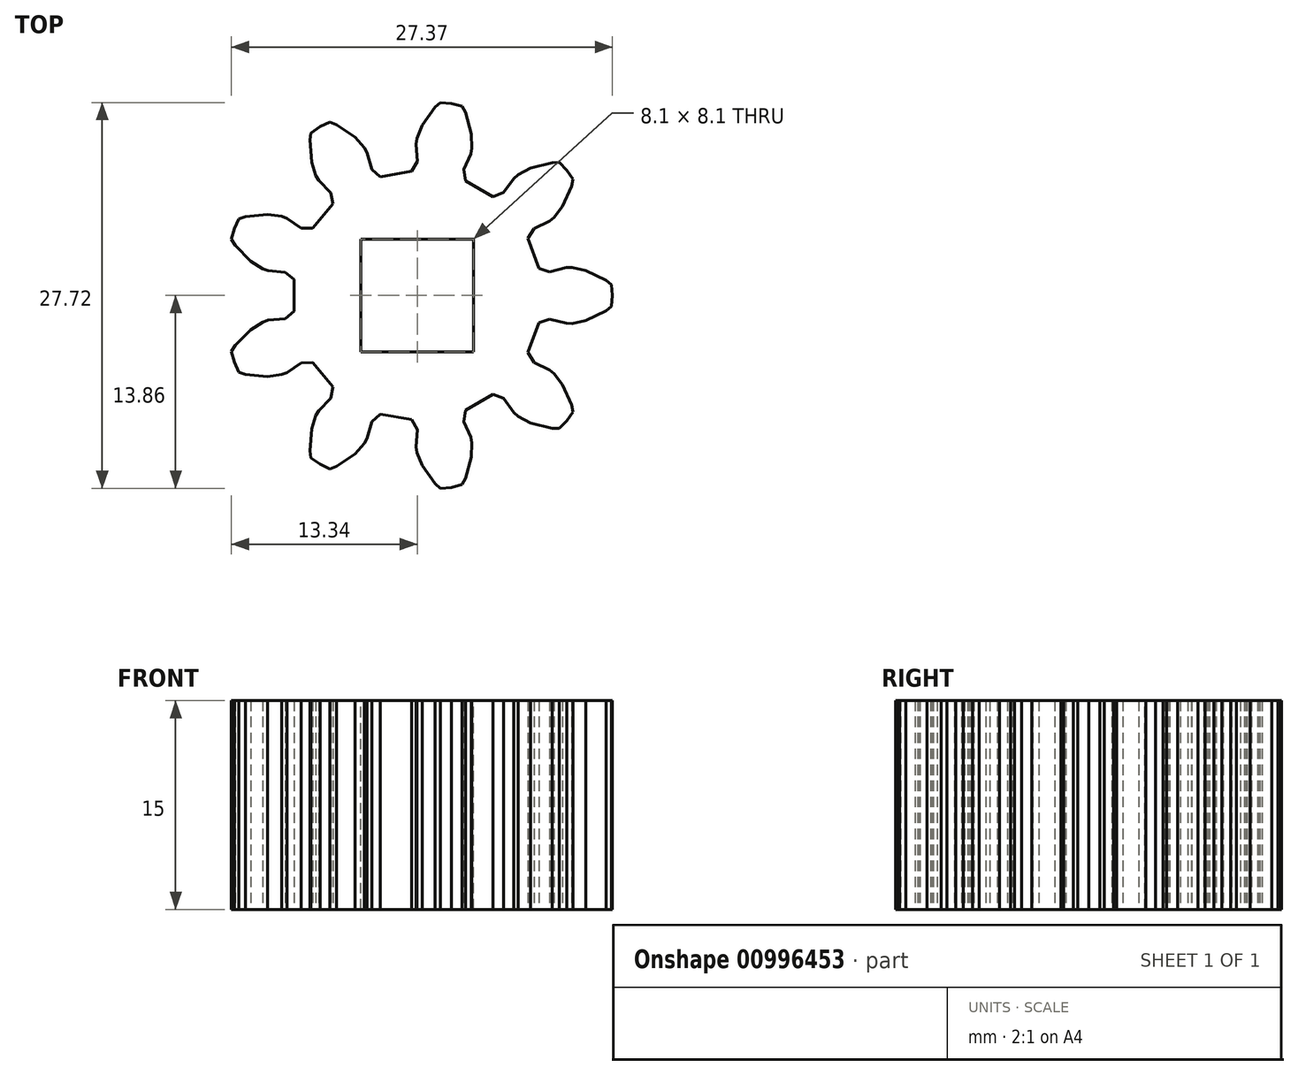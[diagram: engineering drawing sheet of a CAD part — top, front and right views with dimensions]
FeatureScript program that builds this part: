
annotation { "Feature Type Name" : "Feature", "Feature Type Description" : "" }
export const myFeature = defineFeature(function(context is Context, id is Id, definition is map)
    precondition{}
    {
        {
            var Q0;
            Q0=qCreatedBy(makeId("Top.planeOp"),FACE);
            var sketch = newSketch(context, id + "F0", { "sketchPlane" : qUnion([Q0])});
            skLineSegment(sketch, "E0", {"start": v(10.2, -9.56) * mm, "end": v(10.75, -9) * mm});
            skLineSegment(sketch, "E1", {"start": v(10.75, -9) * mm, "end": v(11.2, -8.36) * mm});
            skLineSegment(sketch, "E2", {"start": v(11.2, -8.36) * mm, "end": v(11.1, -7.86) * mm});
            skLineSegment(sketch, "E3", {"start": v(11.1, -7.86) * mm, "end": v(10.44, -6.4) * mm});
            skLineSegment(sketch, "E4", {"start": v(10.44, -6.4) * mm, "end": v(9.83, -5.6) * mm});
            skLineSegment(sketch, "E5", {"start": v(9.83, -5.6) * mm, "end": v(9.5, -5.34) * mm});
            skLineSegment(sketch, "E6", {"start": v(9.5, -5.34) * mm, "end": v(8.38, -4.8) * mm});
            skLineSegment(sketch, "E7", {"start": v(8.38, -4.8) * mm, "end": v(7.96, -4.1) * mm});
            skLineSegment(sketch, "E8", {"start": v(7.96, -4.1) * mm, "end": v(8.74, -1.96) * mm});
            skLineSegment(sketch, "E9", {"start": v(8.74, -1.96) * mm, "end": v(9.52, -1.7) * mm});
            skLineSegment(sketch, "E10", {"start": v(9.52, -1.7) * mm, "end": v(10.72, -2) * mm});
            skLineSegment(sketch, "E11", {"start": v(10.72, -2) * mm, "end": v(11.13, -2) * mm});
            skLineSegment(sketch, "E12", {"start": v(11.13, -2) * mm, "end": v(12.12, -1.8) * mm});
            skLineSegment(sketch, "E13", {"start": v(12.12, -1.8) * mm, "end": v(13.56, -1.1) * mm});
            skLineSegment(sketch, "E14", {"start": v(13.56, -1.1) * mm, "end": v(13.96, -0.79) * mm});
            skLineSegment(sketch, "E15", {"start": v(13.96, -0.79) * mm, "end": v(14.03, 0) * mm});
            skLineSegment(sketch, "E16", {"start": v(14.03, 0) * mm, "end": v(13.96, 0.79) * mm});
            skLineSegment(sketch, "E17", {"start": v(13.96, 0.79) * mm, "end": v(13.56, 1.1) * mm});
            skLineSegment(sketch, "E18", {"start": v(13.56, 1.1) * mm, "end": v(12.12, 1.8) * mm});
            skLineSegment(sketch, "E19", {"start": v(12.12, 1.8) * mm, "end": v(11.13, 2) * mm});
            skLineSegment(sketch, "E20", {"start": v(11.13, 2) * mm, "end": v(10.72, 2) * mm});
            skLineSegment(sketch, "E21", {"start": v(10.72, 2) * mm, "end": v(9.52, 1.7) * mm});
            skLineSegment(sketch, "E22", {"start": v(9.52, 1.7) * mm, "end": v(8.74, 1.96) * mm});
            skLineSegment(sketch, "E23", {"start": v(8.74, 1.96) * mm, "end": v(7.96, 4.1) * mm});
            skLineSegment(sketch, "E24", {"start": v(7.96, 4.1) * mm, "end": v(8.38, 4.8) * mm});
            skLineSegment(sketch, "E25", {"start": v(8.38, 4.8) * mm, "end": v(9.5, 5.34) * mm});
            skLineSegment(sketch, "E26", {"start": v(9.5, 5.34) * mm, "end": v(9.83, 5.6) * mm});
            skLineSegment(sketch, "E27", {"start": v(9.83, 5.6) * mm, "end": v(10.44, 6.4) * mm});
            skLineSegment(sketch, "E28", {"start": v(10.44, 6.4) * mm, "end": v(11.1, 7.86) * mm});
            skLineSegment(sketch, "E29", {"start": v(11.1, 7.86) * mm, "end": v(11.2, 8.36) * mm});
            skLineSegment(sketch, "E30", {"start": v(11.2, 8.36) * mm, "end": v(10.75, 9) * mm});
            skLineSegment(sketch, "E31", {"start": v(10.75, 9) * mm, "end": v(10.2, 9.56) * mm});
            skLineSegment(sketch, "E32", {"start": v(10.2, 9.56) * mm, "end": v(9.68, 9.55) * mm});
            skLineSegment(sketch, "E33", {"start": v(9.68, 9.55) * mm, "end": v(8.14, 9.15) * mm});
            skLineSegment(sketch, "E34", {"start": v(8.14, 9.15) * mm, "end": v(7.24, 8.68) * mm});
            skLineSegment(sketch, "E35", {"start": v(7.24, 8.68) * mm, "end": v(6.93, 8.4) * mm});
            skLineSegment(sketch, "E36", {"start": v(6.93, 8.4) * mm, "end": v(6.2, 7.4) * mm});
            skLineSegment(sketch, "E37", {"start": v(6.2, 7.4) * mm, "end": v(5.44, 7.1) * mm});
            skLineSegment(sketch, "E38", {"start": v(5.44, 7.1) * mm, "end": v(3.47, 8.24) * mm});
            skLineSegment(sketch, "E39", {"start": v(3.47, 8.24) * mm, "end": v(3.34, 9.06) * mm});
            skLineSegment(sketch, "E40", {"start": v(3.34, 9.06) * mm, "end": v(3.85, 10.18) * mm});
            skLineSegment(sketch, "E41", {"start": v(3.85, 10.18) * mm, "end": v(3.93, 10.6) * mm});
            skLineSegment(sketch, "E42", {"start": v(3.93, 10.6) * mm, "end": v(3.89, 11.6) * mm});
            skLineSegment(sketch, "E43", {"start": v(3.89, 11.6) * mm, "end": v(3.46, 13.14) * mm});
            skLineSegment(sketch, "E44", {"start": v(3.46, 13.14) * mm, "end": v(3.22, 13.59) * mm});
            skLineSegment(sketch, "E45", {"start": v(3.22, 13.59) * mm, "end": v(2.45, 13.8) * mm});
            skLineSegment(sketch, "E46", {"start": v(2.45, 13.8) * mm, "end": v(1.67, 13.86) * mm});
            skLineSegment(sketch, "E47", {"start": v(1.67, 13.86) * mm, "end": v(1.28, 13.53) * mm});
            skLineSegment(sketch, "E48", {"start": v(1.28, 13.53) * mm, "end": v(0.35, 12.23) * mm});
            skLineSegment(sketch, "E49", {"start": v(0.35, 12.23) * mm, "end": v(-0.03, 11.3) * mm});
            skLineSegment(sketch, "E50", {"start": v(-0.03, 11.3) * mm, "end": v(-0.1, 10.88) * mm});
            skLineSegment(sketch, "E51", {"start": v(-0.1, 10.88) * mm, "end": v(0, 9.65) * mm});
            skLineSegment(sketch, "E52", {"start": v(0, 9.65) * mm, "end": v(-0.4, 8.93) * mm});
            skLineSegment(sketch, "E53", {"start": v(-0.4, 8.93) * mm, "end": v(-2.64, 8.53) * mm});
            skLineSegment(sketch, "E54", {"start": v(-2.64, 8.53) * mm, "end": v(-3.26, 9.07) * mm});
            skLineSegment(sketch, "E55", {"start": v(-3.26, 9.07) * mm, "end": v(-3.6, 10.26) * mm});
            skLineSegment(sketch, "E56", {"start": v(-3.6, 10.26) * mm, "end": v(-3.8, 10.63) * mm});
            skLineSegment(sketch, "E57", {"start": v(-3.8, 10.63) * mm, "end": v(-4.47, 11.38) * mm});
            skLineSegment(sketch, "E58", {"start": v(-4.47, 11.38) * mm, "end": v(-5.8, 12.28) * mm});
            skLineSegment(sketch, "E59", {"start": v(-5.8, 12.28) * mm, "end": v(-6.27, 12.46) * mm});
            skLineSegment(sketch, "E60", {"start": v(-6.27, 12.46) * mm, "end": v(-6.98, 12.13) * mm});
            skLineSegment(sketch, "E61", {"start": v(-6.98, 12.13) * mm, "end": v(-7.63, 11.68) * mm});
            skLineSegment(sketch, "E62", {"start": v(-7.63, 11.68) * mm, "end": v(-7.7, 11.17) * mm});
            skLineSegment(sketch, "E63", {"start": v(-7.7, 11.17) * mm, "end": v(-7.58, 9.58) * mm});
            skLineSegment(sketch, "E64", {"start": v(-7.58, 9.58) * mm, "end": v(-7.27, 8.62) * mm});
            skLineSegment(sketch, "E65", {"start": v(-7.27, 8.62) * mm, "end": v(-7.06, 8.26) * mm});
            skLineSegment(sketch, "E66", {"start": v(-7.06, 8.26) * mm, "end": v(-6.2, 7.38) * mm});
            skLineSegment(sketch, "E67", {"start": v(-6.2, 7.38) * mm, "end": v(-6.04, 6.57) * mm});
            skLineSegment(sketch, "E68", {"start": v(-6.04, 6.57) * mm, "end": v(-7.5, 4.82) * mm});
            skLineSegment(sketch, "E69", {"start": v(-7.5, 4.82) * mm, "end": v(-8.32, 4.84) * mm});
            skLineSegment(sketch, "E70", {"start": v(-8.32, 4.84) * mm, "end": v(-9.34, 5.54) * mm});
            skLineSegment(sketch, "E71", {"start": v(-9.34, 5.54) * mm, "end": v(-9.73, 5.69) * mm});
            skLineSegment(sketch, "E72", {"start": v(-9.73, 5.69) * mm, "end": v(-10.73, 5.82) * mm});
            skLineSegment(sketch, "E73", {"start": v(-10.73, 5.82) * mm, "end": v(-12.32, 5.67) * mm});
            skLineSegment(sketch, "E74", {"start": v(-12.32, 5.67) * mm, "end": v(-12.8, 5.5) * mm});
            skLineSegment(sketch, "E75", {"start": v(-12.8, 5.5) * mm, "end": v(-13.14, 4.8) * mm});
            skLineSegment(sketch, "E76", {"start": v(-13.14, 4.8) * mm, "end": v(-13.34, 4.03) * mm});
            skLineSegment(sketch, "E77", {"start": v(-13.34, 4.03) * mm, "end": v(-13.08, 3.6) * mm});
            skLineSegment(sketch, "E78", {"start": v(-13.08, 3.6) * mm, "end": v(-11.96, 2.45) * mm});
            skLineSegment(sketch, "E79", {"start": v(-11.96, 2.45) * mm, "end": v(-11.1, 1.91) * mm});
            skLineSegment(sketch, "E80", {"start": v(-11.1, 1.91) * mm, "end": v(-10.71, 1.78) * mm});
            skLineSegment(sketch, "E81", {"start": v(-10.71, 1.78) * mm, "end": v(-9.48, 1.66) * mm});
            skLineSegment(sketch, "E82", {"start": v(-9.48, 1.66) * mm, "end": v(-8.84, 1.14) * mm});
            skLineSegment(sketch, "E83", {"start": v(-8.84, 1.14) * mm, "end": v(-8.84, -1.14) * mm});
            skLineSegment(sketch, "E84", {"start": v(-8.84, -1.14) * mm, "end": v(-9.48, -1.66) * mm});
            skLineSegment(sketch, "E85", {"start": v(-9.48, -1.66) * mm, "end": v(-10.71, -1.78) * mm});
            skLineSegment(sketch, "E86", {"start": v(-10.71, -1.78) * mm, "end": v(-11.1, -1.91) * mm});
            skLineSegment(sketch, "E87", {"start": v(-11.1, -1.91) * mm, "end": v(-11.96, -2.45) * mm});
            skLineSegment(sketch, "E88", {"start": v(-11.96, -2.45) * mm, "end": v(-13.08, -3.6) * mm});
            skLineSegment(sketch, "E89", {"start": v(-13.08, -3.6) * mm, "end": v(-13.34, -4.03) * mm});
            skLineSegment(sketch, "E90", {"start": v(-13.34, -4.03) * mm, "end": v(-13.14, -4.8) * mm});
            skLineSegment(sketch, "E91", {"start": v(-13.14, -4.8) * mm, "end": v(-12.8, -5.5) * mm});
            skLineSegment(sketch, "E92", {"start": v(-12.8, -5.5) * mm, "end": v(-12.32, -5.67) * mm});
            skLineSegment(sketch, "E93", {"start": v(-12.32, -5.67) * mm, "end": v(-10.73, -5.82) * mm});
            skLineSegment(sketch, "E94", {"start": v(-10.73, -5.82) * mm, "end": v(-9.73, -5.69) * mm});
            skLineSegment(sketch, "E95", {"start": v(-9.73, -5.69) * mm, "end": v(-9.34, -5.54) * mm});
            skLineSegment(sketch, "E96", {"start": v(-9.34, -5.54) * mm, "end": v(-8.32, -4.84) * mm});
            skLineSegment(sketch, "E97", {"start": v(-8.32, -4.84) * mm, "end": v(-7.5, -4.82) * mm});
            skLineSegment(sketch, "E98", {"start": v(-7.5, -4.82) * mm, "end": v(-6.04, -6.57) * mm});
            skLineSegment(sketch, "E99", {"start": v(-6.04, -6.57) * mm, "end": v(-6.2, -7.38) * mm});
            skLineSegment(sketch, "E100", {"start": v(-6.2, -7.38) * mm, "end": v(-7.06, -8.26) * mm});
            skLineSegment(sketch, "E101", {"start": v(-7.06, -8.26) * mm, "end": v(-7.27, -8.62) * mm});
            skLineSegment(sketch, "E102", {"start": v(-7.27, -8.62) * mm, "end": v(-7.58, -9.58) * mm});
            skLineSegment(sketch, "E103", {"start": v(-7.58, -9.58) * mm, "end": v(-7.7, -11.17) * mm});
            skLineSegment(sketch, "E104", {"start": v(-7.7, -11.17) * mm, "end": v(-7.63, -11.68) * mm});
            skLineSegment(sketch, "E105", {"start": v(-7.63, -11.68) * mm, "end": v(-6.98, -12.13) * mm});
            skLineSegment(sketch, "E106", {"start": v(-6.98, -12.13) * mm, "end": v(-6.27, -12.46) * mm});
            skLineSegment(sketch, "E107", {"start": v(-6.27, -12.46) * mm, "end": v(-5.8, -12.28) * mm});
            skLineSegment(sketch, "E108", {"start": v(-5.8, -12.28) * mm, "end": v(-4.47, -11.38) * mm});
            skLineSegment(sketch, "E109", {"start": v(-4.47, -11.38) * mm, "end": v(-3.8, -10.63) * mm});
            skLineSegment(sketch, "E110", {"start": v(-3.8, -10.63) * mm, "end": v(-3.6, -10.26) * mm});
            skLineSegment(sketch, "E111", {"start": v(-3.6, -10.26) * mm, "end": v(-3.26, -9.07) * mm});
            skLineSegment(sketch, "E112", {"start": v(-3.26, -9.07) * mm, "end": v(-2.64, -8.53) * mm});
            skLineSegment(sketch, "E113", {"start": v(-2.64, -8.53) * mm, "end": v(-0.4, -8.93) * mm});
            skLineSegment(sketch, "E114", {"start": v(-0.4, -8.93) * mm, "end": v(0, -9.65) * mm});
            skLineSegment(sketch, "E115", {"start": v(0, -9.65) * mm, "end": v(-0.1, -10.88) * mm});
            skLineSegment(sketch, "E116", {"start": v(-0.1, -10.88) * mm, "end": v(-0.03, -11.3) * mm});
            skLineSegment(sketch, "E117", {"start": v(-0.03, -11.3) * mm, "end": v(0.35, -12.23) * mm});
            skLineSegment(sketch, "E118", {"start": v(0.35, -12.23) * mm, "end": v(1.28, -13.53) * mm});
            skLineSegment(sketch, "E119", {"start": v(1.28, -13.53) * mm, "end": v(1.67, -13.86) * mm});
            skLineSegment(sketch, "E120", {"start": v(1.67, -13.86) * mm, "end": v(2.45, -13.8) * mm});
            skLineSegment(sketch, "E121", {"start": v(2.45, -13.8) * mm, "end": v(3.22, -13.59) * mm});
            skLineSegment(sketch, "E122", {"start": v(3.22, -13.59) * mm, "end": v(3.46, -13.14) * mm});
            skLineSegment(sketch, "E123", {"start": v(3.46, -13.14) * mm, "end": v(3.89, -11.6) * mm});
            skLineSegment(sketch, "E124", {"start": v(3.89, -11.6) * mm, "end": v(3.93, -10.6) * mm});
            skLineSegment(sketch, "E125", {"start": v(3.93, -10.6) * mm, "end": v(3.85, -10.18) * mm});
            skLineSegment(sketch, "E126", {"start": v(3.85, -10.18) * mm, "end": v(3.34, -9.06) * mm});
            skLineSegment(sketch, "E127", {"start": v(3.34, -9.06) * mm, "end": v(3.47, -8.24) * mm});
            skLineSegment(sketch, "E128", {"start": v(3.47, -8.24) * mm, "end": v(5.44, -7.1) * mm});
            skLineSegment(sketch, "E129", {"start": v(5.44, -7.1) * mm, "end": v(6.2, -7.4) * mm});
            skLineSegment(sketch, "E130", {"start": v(6.2, -7.4) * mm, "end": v(6.93, -8.4) * mm});
            skLineSegment(sketch, "E131", {"start": v(6.93, -8.4) * mm, "end": v(7.24, -8.68) * mm});
            skLineSegment(sketch, "E132", {"start": v(7.24, -8.68) * mm, "end": v(8.14, -9.15) * mm});
            skLineSegment(sketch, "E133", {"start": v(8.14, -9.15) * mm, "end": v(9.68, -9.55) * mm});
            skLineSegment(sketch, "E134", {"start": v(9.68, -9.55) * mm, "end": v(10.2, -9.56) * mm});
            skSolve(sketch);
        }
        {
            var Q0;
            Q0=qSketchRegion(id+"F0",true);
            extrude(context, id + "F1", {"entities" : qUnion([Q0]), "depth" : 15 * mm, "offsetDistance" : 25.4 * mm});
        }
        {
            var Q0;
            Q0=makeQuery(id+"F1.opExtrude","CAP_FACE",FACE,{"disambiguationData":[OSD([sQuery(id+"F0.wireOp",EDGE,"E0"),sQuery(id+"F0.wireOp",EDGE,"E1"),sQuery(id+"F0.wireOp",EDGE,"E2"),sQuery(id+"F0.wireOp",EDGE,"E3"),sQuery(id+"F0.wireOp",EDGE,"E4"),sQuery(id+"F0.wireOp",EDGE,"E5"),sQuery(id+"F0.wireOp",EDGE,"E6"),sQuery(id+"F0.wireOp",EDGE,"E7"),sQuery(id+"F0.wireOp",EDGE,"E8"),sQuery(id+"F0.wireOp",EDGE,"E9"),sQuery(id+"F0.wireOp",EDGE,"E10"),sQuery(id+"F0.wireOp",EDGE,"E11"),sQuery(id+"F0.wireOp",EDGE,"E12"),sQuery(id+"F0.wireOp",EDGE,"E13"),sQuery(id+"F0.wireOp",EDGE,"E14"),sQuery(id+"F0.wireOp",EDGE,"E15"),sQuery(id+"F0.wireOp",EDGE,"E16"),sQuery(id+"F0.wireOp",EDGE,"E17"),sQuery(id+"F0.wireOp",EDGE,"E18"),sQuery(id+"F0.wireOp",EDGE,"E19"),sQuery(id+"F0.wireOp",EDGE,"E20"),sQuery(id+"F0.wireOp",EDGE,"E21"),sQuery(id+"F0.wireOp",EDGE,"E22"),sQuery(id+"F0.wireOp",EDGE,"E23"),sQuery(id+"F0.wireOp",EDGE,"E24"),sQuery(id+"F0.wireOp",EDGE,"E25"),sQuery(id+"F0.wireOp",EDGE,"E26"),sQuery(id+"F0.wireOp",EDGE,"E27"),sQuery(id+"F0.wireOp",EDGE,"E28"),sQuery(id+"F0.wireOp",EDGE,"E29"),sQuery(id+"F0.wireOp",EDGE,"E30"),sQuery(id+"F0.wireOp",EDGE,"E31"),sQuery(id+"F0.wireOp",EDGE,"E32"),sQuery(id+"F0.wireOp",EDGE,"E33"),sQuery(id+"F0.wireOp",EDGE,"E34"),sQuery(id+"F0.wireOp",EDGE,"E35"),sQuery(id+"F0.wireOp",EDGE,"E36"),sQuery(id+"F0.wireOp",EDGE,"E37"),sQuery(id+"F0.wireOp",EDGE,"E38"),sQuery(id+"F0.wireOp",EDGE,"E39"),sQuery(id+"F0.wireOp",EDGE,"E40"),sQuery(id+"F0.wireOp",EDGE,"E41"),sQuery(id+"F0.wireOp",EDGE,"E42"),sQuery(id+"F0.wireOp",EDGE,"E43"),sQuery(id+"F0.wireOp",EDGE,"E44"),sQuery(id+"F0.wireOp",EDGE,"E45"),sQuery(id+"F0.wireOp",EDGE,"E46"),sQuery(id+"F0.wireOp",EDGE,"E47"),sQuery(id+"F0.wireOp",EDGE,"E48"),sQuery(id+"F0.wireOp",EDGE,"E49"),sQuery(id+"F0.wireOp",EDGE,"E50"),sQuery(id+"F0.wireOp",EDGE,"E51"),sQuery(id+"F0.wireOp",EDGE,"E52"),sQuery(id+"F0.wireOp",EDGE,"E53"),sQuery(id+"F0.wireOp",EDGE,"E54"),sQuery(id+"F0.wireOp",EDGE,"E55"),sQuery(id+"F0.wireOp",EDGE,"E56"),sQuery(id+"F0.wireOp",EDGE,"E57"),sQuery(id+"F0.wireOp",EDGE,"E58"),sQuery(id+"F0.wireOp",EDGE,"E59"),sQuery(id+"F0.wireOp",EDGE,"E60"),sQuery(id+"F0.wireOp",EDGE,"E61"),sQuery(id+"F0.wireOp",EDGE,"E62"),sQuery(id+"F0.wireOp",EDGE,"E63"),sQuery(id+"F0.wireOp",EDGE,"E64"),sQuery(id+"F0.wireOp",EDGE,"E65"),sQuery(id+"F0.wireOp",EDGE,"E66"),sQuery(id+"F0.wireOp",EDGE,"E67"),sQuery(id+"F0.wireOp",EDGE,"E68"),sQuery(id+"F0.wireOp",EDGE,"E69"),sQuery(id+"F0.wireOp",EDGE,"E70"),sQuery(id+"F0.wireOp",EDGE,"E71"),sQuery(id+"F0.wireOp",EDGE,"E72"),sQuery(id+"F0.wireOp",EDGE,"E73"),sQuery(id+"F0.wireOp",EDGE,"E74"),sQuery(id+"F0.wireOp",EDGE,"E75"),sQuery(id+"F0.wireOp",EDGE,"E76"),sQuery(id+"F0.wireOp",EDGE,"E77"),sQuery(id+"F0.wireOp",EDGE,"E78"),sQuery(id+"F0.wireOp",EDGE,"E79"),sQuery(id+"F0.wireOp",EDGE,"E80"),sQuery(id+"F0.wireOp",EDGE,"E81"),sQuery(id+"F0.wireOp",EDGE,"E82"),sQuery(id+"F0.wireOp",EDGE,"E83"),sQuery(id+"F0.wireOp",EDGE,"E84"),sQuery(id+"F0.wireOp",EDGE,"E85"),sQuery(id+"F0.wireOp",EDGE,"E86"),sQuery(id+"F0.wireOp",EDGE,"E87"),sQuery(id+"F0.wireOp",EDGE,"E88"),sQuery(id+"F0.wireOp",EDGE,"E89"),sQuery(id+"F0.wireOp",EDGE,"E90"),sQuery(id+"F0.wireOp",EDGE,"E91"),sQuery(id+"F0.wireOp",EDGE,"E92"),sQuery(id+"F0.wireOp",EDGE,"E93"),sQuery(id+"F0.wireOp",EDGE,"E94"),sQuery(id+"F0.wireOp",EDGE,"E95"),sQuery(id+"F0.wireOp",EDGE,"E96"),sQuery(id+"F0.wireOp",EDGE,"E97"),sQuery(id+"F0.wireOp",EDGE,"E98"),sQuery(id+"F0.wireOp",EDGE,"E99"),sQuery(id+"F0.wireOp",EDGE,"E100"),sQuery(id+"F0.wireOp",EDGE,"E101"),sQuery(id+"F0.wireOp",EDGE,"E102"),sQuery(id+"F0.wireOp",EDGE,"E103"),sQuery(id+"F0.wireOp",EDGE,"E104"),sQuery(id+"F0.wireOp",EDGE,"E105"),sQuery(id+"F0.wireOp",EDGE,"E106"),sQuery(id+"F0.wireOp",EDGE,"E107"),sQuery(id+"F0.wireOp",EDGE,"E108"),sQuery(id+"F0.wireOp",EDGE,"E109"),sQuery(id+"F0.wireOp",EDGE,"E110"),sQuery(id+"F0.wireOp",EDGE,"E111"),sQuery(id+"F0.wireOp",EDGE,"E112"),sQuery(id+"F0.wireOp",EDGE,"E113"),sQuery(id+"F0.wireOp",EDGE,"E114"),sQuery(id+"F0.wireOp",EDGE,"E115"),sQuery(id+"F0.wireOp",EDGE,"E116"),sQuery(id+"F0.wireOp",EDGE,"E117"),sQuery(id+"F0.wireOp",EDGE,"E118"),sQuery(id+"F0.wireOp",EDGE,"E119"),sQuery(id+"F0.wireOp",EDGE,"E120"),sQuery(id+"F0.wireOp",EDGE,"E121"),sQuery(id+"F0.wireOp",EDGE,"E122"),sQuery(id+"F0.wireOp",EDGE,"E123"),sQuery(id+"F0.wireOp",EDGE,"E124"),sQuery(id+"F0.wireOp",EDGE,"E125"),sQuery(id+"F0.wireOp",EDGE,"E126"),sQuery(id+"F0.wireOp",EDGE,"E127"),sQuery(id+"F0.wireOp",EDGE,"E128"),sQuery(id+"F0.wireOp",EDGE,"E129"),sQuery(id+"F0.wireOp",EDGE,"E130"),sQuery(id+"F0.wireOp",EDGE,"E131"),sQuery(id+"F0.wireOp",EDGE,"E132"),sQuery(id+"F0.wireOp",EDGE,"E133"),sQuery(id+"F0.wireOp",EDGE,"E134")])],"isStart":false});
            var sketch = newSketch(context, id + "F2", { "sketchPlane" : qUnion([Q0])});
            skLineSegment(sketch, "E135.bottom", {"start": v(4.05, 4.05) * mm, "end": v(-4.05, 4.05) * mm});
            skLineSegment(sketch, "E135.top", {"start": v(4.05, -4.05) * mm, "end": v(-4.05, -4.05) * mm});
            skLineSegment(sketch, "E135.left", {"start": v(4.05, 4.05) * mm, "end": v(4.05, -4.05) * mm});
            skLineSegment(sketch, "E135.right", {"start": v(-4.05, 4.05) * mm, "end": v(-4.05, -4.05) * mm});
            skPoint(sketch, "E135.middle", {"position": v(0, 0) * mm});
            skSolve(sketch);
        }
        {
            var Q0;
            Q0=qSketchRegion(id+"F2",true);
            extrude(context, id + "F3", {"entities" : qUnion([Q0]), "operationType" : NewBodyOperationType.REMOVE, "endBound" : BoundingType.THROUGH_ALL, "oppositeDirection" : true, "depth" : 25 * mm, "offsetDistance" : 25 * mm});
        }
    });
